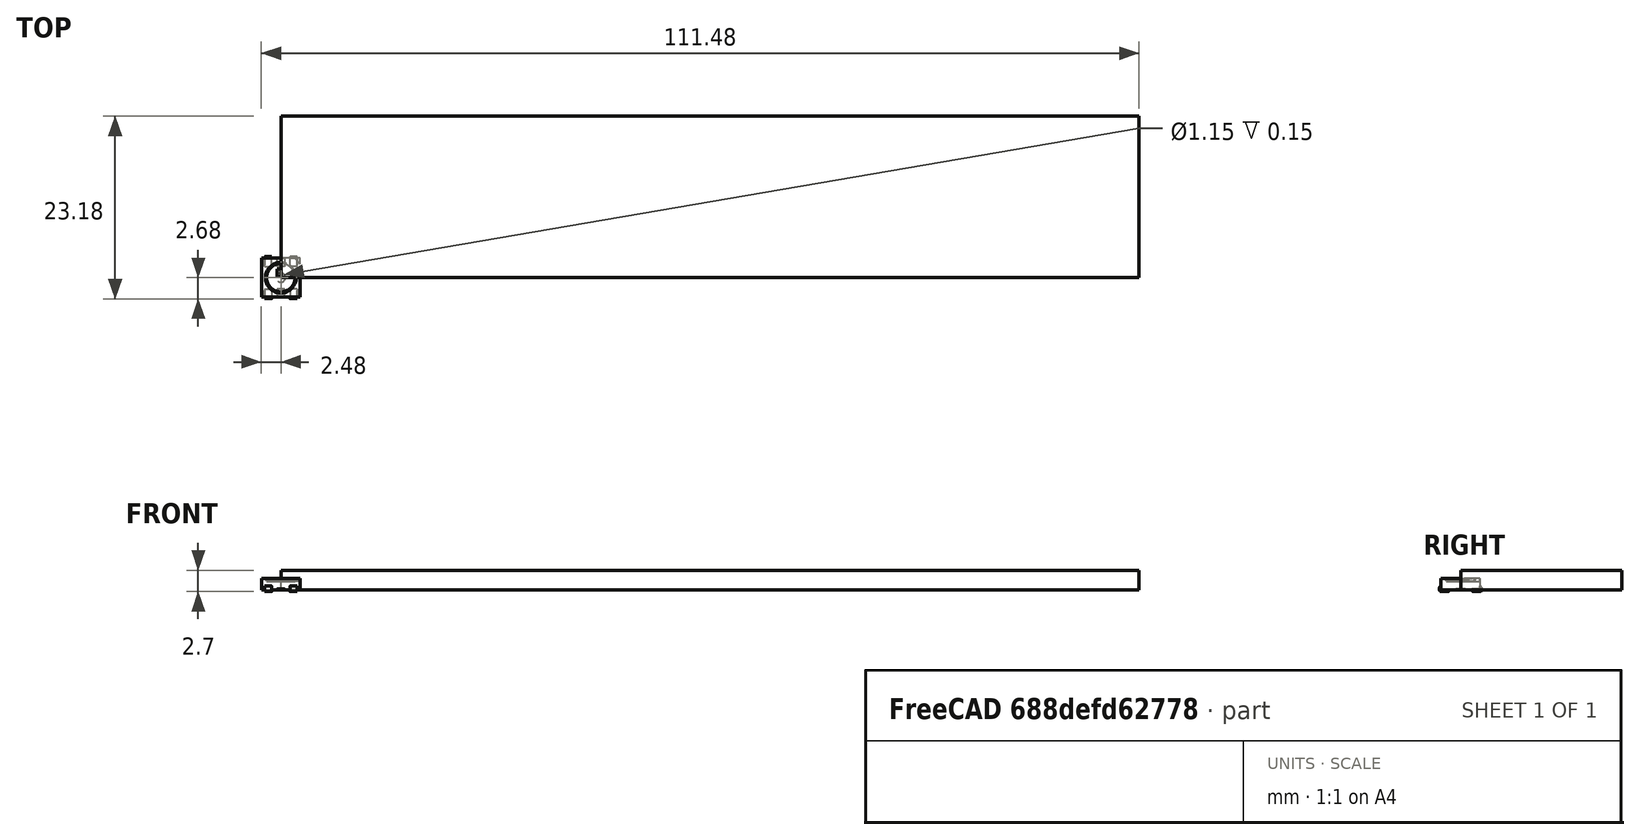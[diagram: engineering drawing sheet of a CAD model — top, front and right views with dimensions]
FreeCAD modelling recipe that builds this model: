
FCSTD DOCUMENT  (FreeCAD 0.21R33771 (Git))
Label: touch_keyboard_led_strip
License: All rights reserved
LicenseURL: http://en.wikipedia.org/wiki/All_rights_reserved
objects: App::Link×2, Part::FeaturePython×2, App::Part×2, PartDesign::CoordinateSystem×2, Part::Feature×1, Spreadsheet::Sheet×1, Part::Box×1
note: 4 computed .brp shape members not serialized (recipe doc carries the construction recipe); baked Part::Feature solids carry a one-line shape summary decoded from their .brp

FEATURE [Part::Feature] Part__Feature  label="WS2812B"
  shape: bbox 4.95 x 5.35 x 1.7 mm, 58 faces (baked)
FEATURE [Spreadsheet::Sheet] Spreadsheet  label="D"
  cells = A2='strip width; B2(width)==20.5 mm; A3='strip length; B3(length)==109 mm; A4='plate height; B4(plate_height)==2.5 mm; A5='top LEDS; B5(top_leds)=9; A6='bottom LEDS; B6(bottom_leds)=10; A7='LED x interval; B7(led_x_interval)==10.3 mm; A8='bottom LED x; B8(bot_led_x)==8.5 mm; A9='bottom LED y; B9(bot_led_y)==5.3 mm; A10='top LED x; B10(top_led_x)==bot_led_x + led_x_interval / 2; A11='top LED y; B11(top_led_y)==14.8 mm
FEATURE [Part::Box] Box  label="Cube"
  AttacherType = Attacher::AttachEngine3D
  Height = 2.5
  Length = 109
  Width = 20.5
  expr: Height = <<D>>.plate_height
  expr: Length = <<D>>.length
  expr: Width = <<D>>.width
FEATURE [App::Link] Link  label="WS2812B001"
  LinkPlacement = pos=(8.5,5.3,2.5) rot=(0,0,1;3.14159rad)
  LinkedObject = -> Part__Feature
  Placement = pos=(8.5,5.3,2.5) rot=(0,0,1;3.14159rad)
  expr: .Placement.Base.x = <<D>>.bot_led_x
  expr: .Placement.Base.y = <<D>>.bot_led_y
  expr: .Placement.Base.z = <<D>>.plate_height
FEATURE [Part::FeaturePython] Array  # Draft array (typed FeaturePython)
  AlwaysSyncPlacement = false
  Angle = 360
  ArrayType = 0
  Axis = (0,0,1)
  Base = -> Link
  Center = (0,0,0)
  Count = 10
  ExpandArray = false
  Fuse = false
  IntervalAxis = (0,0,0)
  IntervalX = (10.3,0,0)
  IntervalY = (0,100,0)
  IntervalZ = (0,0,100)
  NumberCircles = 3
  NumberPolar = 5
  NumberX = 10
  NumberY = 1
  NumberZ = 1
  PlacementList = 10 placements: arithmetic series from (8.5,5.3,2.5) step (10.3,0,0) to (101.2,5.3,2.5)
  RadialDistance = 50
  ScaleList = (10) [(1,1,1),(1,1,1),(1,1,1),(1,1,1),(1,1,1),(1,1,1),(1,1,1),(1,1,1),(1,1,1),(1,1,1)]
  Symmetry = 1
  TangentialDistance = 25
FEATURE [App::Link] Link001  label="WS2812B002"
  LinkPlacement = pos=(13.65,14.8,2.5) rot=(0,0,1;0rad)
  LinkedObject = -> Part__Feature
  Placement = pos=(13.65,14.8,2.5) rot=(0,0,1;0rad)
  expr: .Placement.Base.x = <<D>>.top_led_x
  expr: .Placement.Base.y = <<D>>.top_led_y
  expr: .Placement.Base.z = <<D>>.plate_height
FEATURE [Part::FeaturePython] Array001  # Draft array (typed FeaturePython)
  AlwaysSyncPlacement = false
  Angle = 360
  ArrayType = 0
  Axis = (0,0,1)
  Base = -> Link001
  Center = (0,0,0)
  Count = 9
  ExpandArray = false
  Fuse = false
  IntervalAxis = (0,0,0)
  IntervalX = (10.3,0,0)
  IntervalY = (0,100,0)
  IntervalZ = (0,0,100)
  NumberCircles = 3
  NumberPolar = 5
  NumberX = 9
  NumberY = 1
  NumberZ = 1
  PlacementList = 9 placements: arithmetic series from (13.65,14.8,2.5) step (10.3,0,0) to (96.05,14.8,2.5)
  RadialDistance = 50
  ScaleList = (9) [(1,1,1),(1,1,1),(1,1,1),(1,1,1),(1,1,1),(1,1,1),(1,1,1),(1,1,1),(1,1,1)]
  Symmetry = 1
  TangentialDistance = 25
FEATURE [App::Part] Part001  label="Plate"
  Group = -> [Box,Link,Array,Link001,Array001]
  Origin = -> Origin001
FEATURE [PartDesign::CoordinateSystem] Botom_Left
  AttacherType = Attacher::AttachEngine3D
  MapMode = 2
  Support = -> [Part001]
FEATURE [PartDesign::CoordinateSystem] Bottom_middle
  AttacherType = Attacher::AttachEngine3D
  AttachmentOffset = pos=(54.5,0,0) rot=(0,0,1;0rad)
  MapMode = 2
  Placement = pos=(54.5,0,0) rot=(0,0,1;0rad)
  Support = -> [Part001]
  expr: .AttachmentOffset.Base.x = <<D>>.length / 2
FEATURE [App::Part] Part  label="LED Strip"
  Group = -> [Part001,Part__Feature,Botom_Left,Bottom_middle]
  Origin = -> Origin
